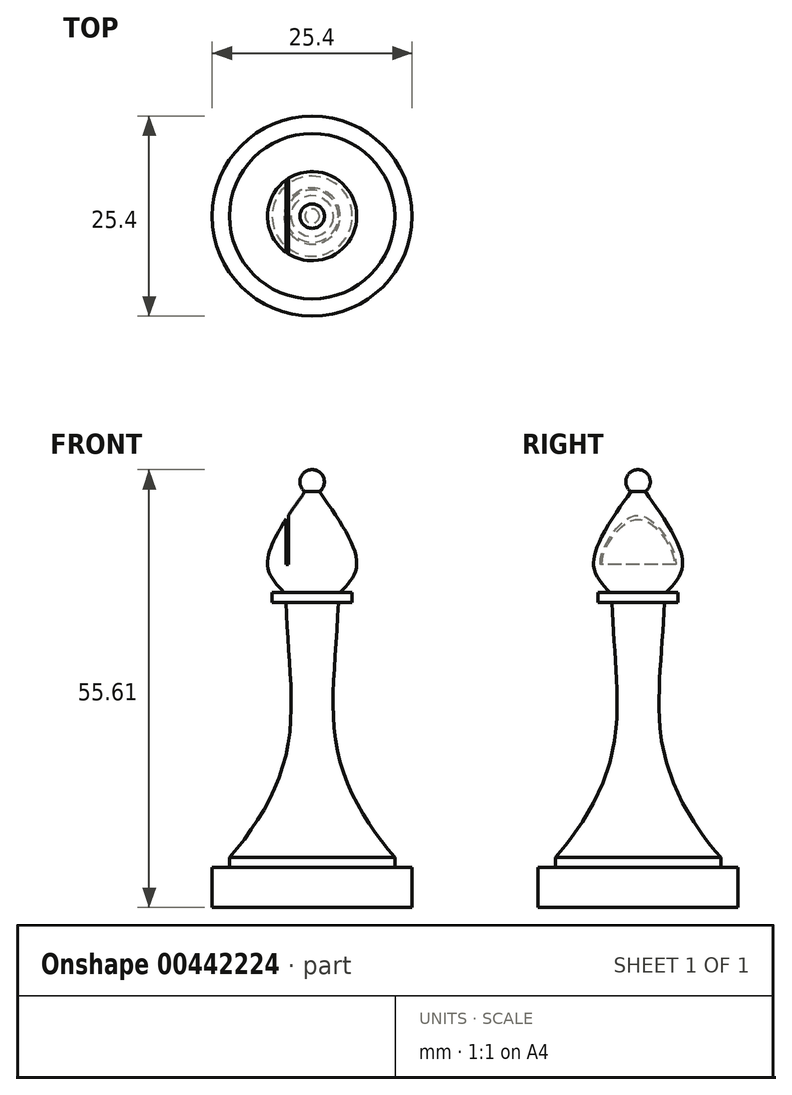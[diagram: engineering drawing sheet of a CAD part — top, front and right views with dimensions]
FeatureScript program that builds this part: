
annotation { "Feature Type Name" : "Feature", "Feature Type Description" : "" }
export const myFeature = defineFeature(function(context is Context, id is Id, definition is map)
    precondition{}
    {
        {
            var Q0;
            Q0=qCreatedBy(makeId("Front.planeOp"),FACE);
            var sketch = newSketch(context, id + "F0", { "sketchPlane" : qUnion([Q0])});
            skLineSegment(sketch, "E0", {"start": v(0, 20.34) * mm, "end": v(0, -9.5) * mm, "construction": true});
            skLineSegment(sketch, "E1.bottom", {"start": v(0, 0) * mm, "end": v(-12.7, 0) * mm});
            skLineSegment(sketch, "E1.top", {"start": v(0, 5.08) * mm, "end": v(-12.7, 5.08) * mm});
            skLineSegment(sketch, "E1.left", {"start": v(0, 0) * mm, "end": v(0, 5.08) * mm});
            skLineSegment(sketch, "E1.right", {"start": v(-12.7, 0) * mm, "end": v(-12.7, 5.08) * mm});
            skLineSegment(sketch, "E2", {"start": v(-10.5, 5.08) * mm, "end": v(-10.5, 6.35) * mm});
            skLineSegment(sketch, "E3", {"start": v(0, 21.75) * mm, "end": v(0, 5.08) * mm});
            skLineSegment(sketch, "E4", {"start": v(0, 27.4) * mm, "end": v(0, 21.75) * mm});
            skFitSpline(sketch, "E5", {"points": [v(-10.5, 6.35) * mm, v(-3.26, 19.7) * mm, v(-3.33, 38.7) * mm], "startDerivative": vector(19.87, 22.34) * mm, "endDerivative": vector(-1.47, 40.58) * mm});
            skLineSegment(sketch, "E6", {"start": v(-3.33, 38.7) * mm, "end": v(0, 38.7) * mm});
            skLineSegment(sketch, "E7", {"start": v(0, 38.7) * mm, "end": v(0, 27.4) * mm});
            skLineSegment(sketch, "E8", {"start": v(-3.33, 38.7) * mm, "end": v(-5.08, 38.7) * mm});
            skLineSegment(sketch, "E9", {"start": v(-5.08, 38.7) * mm, "end": v(-5.08, 39.97) * mm});
            skLineSegment(sketch, "E10", {"start": v(-5.08, 39.97) * mm, "end": v(0, 39.97) * mm});
            skLineSegment(sketch, "E11", {"start": v(0, 39.97) * mm, "end": v(0, 38.7) * mm});
            skSolve(sketch);
        }
        {
            var Q0;
            Q0 = qSketchRegion(id + "F0", true);
            var Q1;
            Q1=sQuery(id+"F0.wireOp",EDGE,"E0");
            revolve(context, id + "F1", {"entities" : qUnion([Q0]), "axis" : qUnion([Q1]), "revolveType" : RevolveType.FULL});
        }
        {
            var Q0;
            Q0=qCreatedBy(makeId("Front.planeOp"),FACE);
            var sketch = newSketch(context, id + "F2", { "sketchPlane" : qUnion([Q0])});
            skLineSegment(sketch, "E12", {"start": v(0, 55.65) * mm, "end": v(0, 54.06) * mm, "construction": true});
            skFitSpline(sketch, "E13", {"points": [v(-3.57, 40.03) * mm, v(-5.66, 43.67) * mm, v(0, 54.06) * mm], "startDerivative": vector(-8.35, 8.48) * mm, "endDerivative": vector(13.63, 18.71) * mm});
            skLineSegment(sketch, "E14", {"start": v(0, 54.06) * mm, "end": v(0, 40.06) * mm});
            skLineSegment(sketch, "E15", {"start": v(0, 40.06) * mm, "end": v(-3.57, 40.03) * mm});
            skArc(sketch, "E16", {"start": v(-0.91, 52.8) * mm, "mid": v(-1.48, 54.54) * mm, "end": v(0, 55.6) * mm});
            skLineSegment(sketch, "E17", {"start": v(0, 55.6) * mm, "end": v(0, 54.06) * mm});
            skSolve(sketch);
        }
        {
            var Q0;
            Q0 = qSketchRegion(id + "F2", true);
            var Q1;
            Q1=sQuery(id+"F2.wireOp",EDGE,"E12");
            revolve(context, id + "F3", {"entities" : qUnion([Q0]), "axis" : qUnion([Q1]), "revolveType" : RevolveType.FULL});
        }
        {
            var Q0;
            Q0=qCreatedBy(makeId("Front.planeOp"),FACE);
            var sketch = newSketch(context, id + "F4", { "sketchPlane" : qUnion([Q0])});
            skLineSegment(sketch, "E18.bottom", {"start": v(-3, 50.77) * mm, "end": v(-3.32, 50.77) * mm});
            skLineSegment(sketch, "E18.top", {"start": v(-3, 43.57) * mm, "end": v(-3.32, 43.57) * mm});
            skLineSegment(sketch, "E18.left", {"start": v(-3, 50.77) * mm, "end": v(-3, 43.57) * mm});
            skLineSegment(sketch, "E18.right", {"start": v(-3.32, 50.77) * mm, "end": v(-3.32, 43.57) * mm});
            skSolve(sketch);
        }
        {
            var Q0;
            Q0=makeQuery(id+"F4.imprint","IMPRINT",FACE,{"disambiguationData":[TD([[makeQuery(id+"F4.imprint","IMPRINT",EDGE,{"derivedFrom":sQuery(id+"F4.wireOp",EDGE,"E18.bottom")}),1.0]])]});
            extrude(context, id + "F5", {"entities" : qUnion([Q0]), "operationType" : NewBodyOperationType.REMOVE, "endBound" : BoundingType.SYMMETRIC, "oppositeDirection" : true, "depth" : 76.2 * mm});
        }
    });
